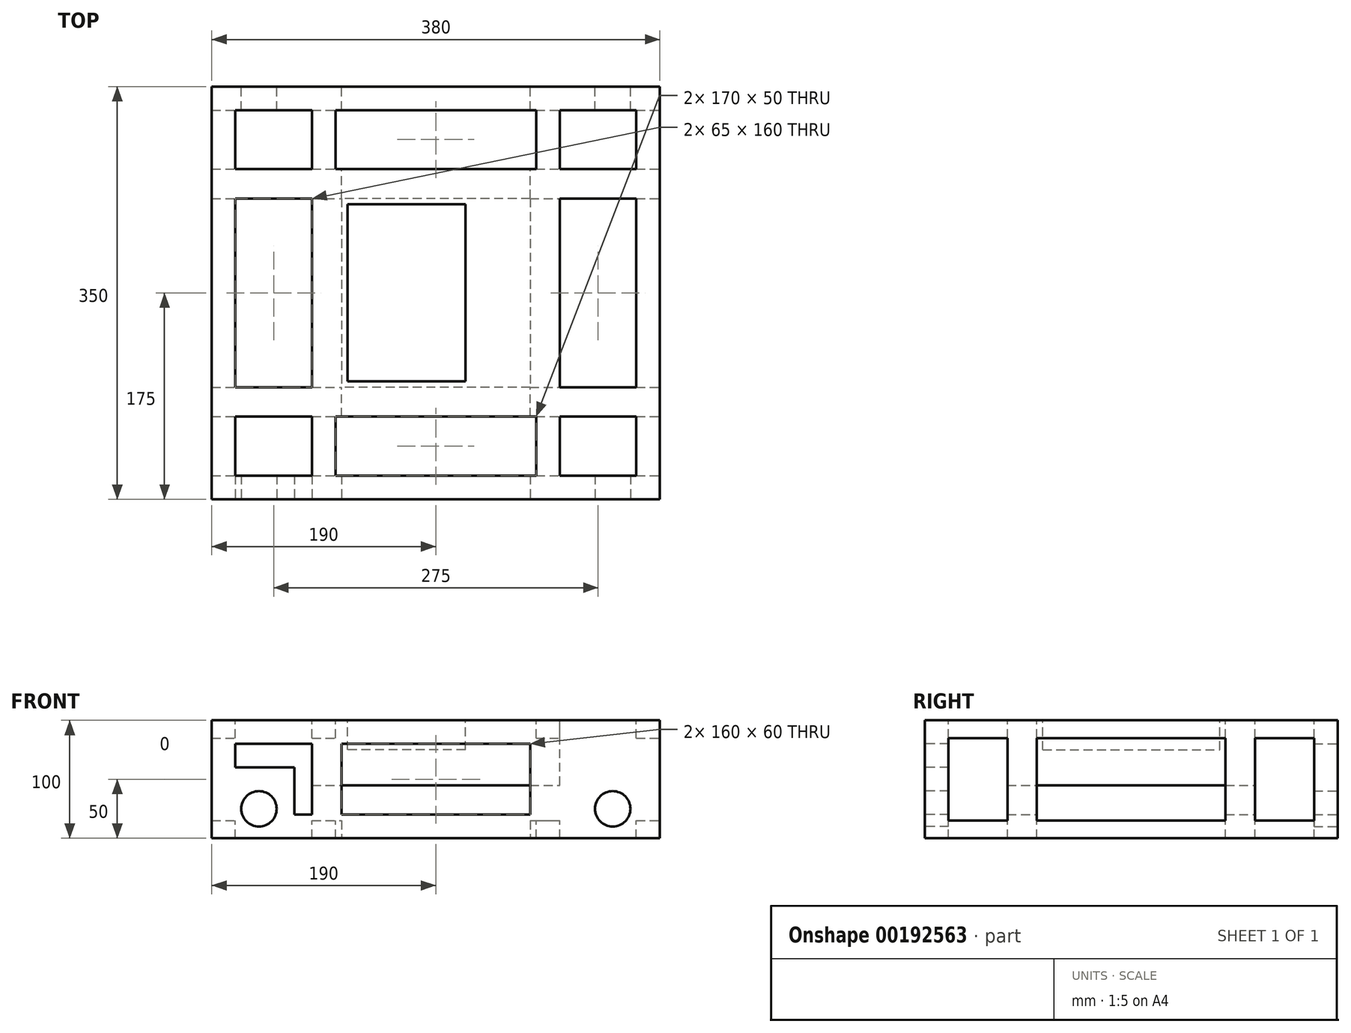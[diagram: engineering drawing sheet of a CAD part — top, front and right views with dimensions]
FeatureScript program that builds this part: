
annotation { "Feature Type Name" : "Feature", "Feature Type Description" : "" }
export const myFeature = defineFeature(function(context is Context, id is Id, definition is map)
    precondition{}
    {
        {
            var Q0;
            Q0=qCreatedBy(makeId("Top.planeOp"),FACE);
            var sketch = newSketch(context, id + "F0", { "sketchPlane" : qUnion([Q0])});
            skLineSegment(sketch, "E0.bottom", {"start": v(190, -175) * mm, "end": v(-190, -175) * mm});
            skLineSegment(sketch, "E0.top", {"start": v(190, 175) * mm, "end": v(-190, 175) * mm});
            skLineSegment(sketch, "E0.left", {"start": v(190, -175) * mm, "end": v(190, 175) * mm});
            skLineSegment(sketch, "E0.right", {"start": v(-190, -175) * mm, "end": v(-190, 175) * mm});
            skPoint(sketch, "E0.middle", {"position": v(0, 0) * mm});
            skSolve(sketch);
        }
        {
            var Q0;
            Q0 = qSketchRegion(id + "F0", true);
            extrude(context, id + "F1", {"entities" : qUnion([Q0]), "depth" : 100 * mm});
        }
        {
            var Q0;
            Q0=makeQuery(id+"F1.opExtrude","CAP_FACE",FACE,{"disambiguationData":[OSD([sQuery(id+"F0.wireOp",EDGE,"E0.bottom"),sQuery(id+"F0.wireOp",EDGE,"E0.top"),sQuery(id+"F0.wireOp",EDGE,"E0.left"),sQuery(id+"F0.wireOp",EDGE,"E0.right")])],"isStart":false});
            var sketch = newSketch(context, id + "F2", { "sketchPlane" : qUnion([Q0])});
            skLineSegment(sketch, "E1.bottom", {"start": v(-85, 155) * mm, "end": v(85, 155) * mm});
            skLineSegment(sketch, "E1.top", {"start": v(-85, 105) * mm, "end": v(85, 105) * mm});
            skLineSegment(sketch, "E1.left", {"start": v(-85, 155) * mm, "end": v(-85, 105) * mm});
            skLineSegment(sketch, "E1.right", {"start": v(85, 155) * mm, "end": v(85, 105) * mm});
            skLineSegment(sketch, "E2.bottom", {"start": v(105, 155) * mm, "end": v(170, 155) * mm});
            skLineSegment(sketch, "E2.top", {"start": v(105, 105) * mm, "end": v(170, 105) * mm});
            skLineSegment(sketch, "E2.left", {"start": v(105, 155) * mm, "end": v(105, 105) * mm});
            skLineSegment(sketch, "E2.right", {"start": v(170, 155) * mm, "end": v(170, 105) * mm});
            skLineSegment(sketch, "E3.bottom", {"start": v(105, 80) * mm, "end": v(170, 80) * mm});
            skLineSegment(sketch, "E3.top", {"start": v(105, -80) * mm, "end": v(170, -80) * mm});
            skLineSegment(sketch, "E3.left", {"start": v(105, 80) * mm, "end": v(105, -80) * mm});
            skLineSegment(sketch, "E3.right", {"start": v(170, 80) * mm, "end": v(170, -80) * mm});
            skLineSegment(sketch, "E4.bottom", {"start": v(105, -105) * mm, "end": v(170, -105) * mm});
            skLineSegment(sketch, "E4.top", {"start": v(105, -155) * mm, "end": v(170, -155) * mm});
            skLineSegment(sketch, "E4.left", {"start": v(105, -105) * mm, "end": v(105, -155) * mm});
            skLineSegment(sketch, "E4.right", {"start": v(170, -105) * mm, "end": v(170, -155) * mm});
            skLineSegment(sketch, "E5.bottom", {"start": v(85, -155) * mm, "end": v(-85, -155) * mm});
            skLineSegment(sketch, "E5.top", {"start": v(85, -105) * mm, "end": v(-85, -105) * mm});
            skLineSegment(sketch, "E5.left", {"start": v(85, -155) * mm, "end": v(85, -105) * mm});
            skLineSegment(sketch, "E5.right", {"start": v(-85, -155) * mm, "end": v(-85, -105) * mm});
            skLineSegment(sketch, "E6.bottom", {"start": v(-170, -105) * mm, "end": v(-105, -105) * mm});
            skLineSegment(sketch, "E6.top", {"start": v(-170, -155) * mm, "end": v(-105, -155) * mm});
            skLineSegment(sketch, "E6.left", {"start": v(-170, -105) * mm, "end": v(-170, -155) * mm});
            skLineSegment(sketch, "E6.right", {"start": v(-105, -105) * mm, "end": v(-105, -155) * mm});
            skLineSegment(sketch, "E7.bottom", {"start": v(-170, -80) * mm, "end": v(-105, -80) * mm});
            skLineSegment(sketch, "E7.top", {"start": v(-170, 80) * mm, "end": v(-105, 80) * mm});
            skLineSegment(sketch, "E7.left", {"start": v(-170, -80) * mm, "end": v(-170, 80) * mm});
            skLineSegment(sketch, "E7.right", {"start": v(-105, -80) * mm, "end": v(-105, 80) * mm});
            skLineSegment(sketch, "E8.bottom", {"start": v(-170, 155) * mm, "end": v(-105, 155) * mm});
            skLineSegment(sketch, "E8.top", {"start": v(-170, 105) * mm, "end": v(-105, 105) * mm});
            skLineSegment(sketch, "E8.left", {"start": v(-170, 155) * mm, "end": v(-170, 105) * mm});
            skLineSegment(sketch, "E8.right", {"start": v(-105, 155) * mm, "end": v(-105, 105) * mm});
            skSolve(sketch);
        }
        {
            var Q0;
            Q0 = qSketchRegion(id + "F2", true);
            extrude(context, id + "F3", {"entities" : qUnion([Q0]), "operationType" : NewBodyOperationType.REMOVE, "endBound" : BoundingType.THROUGH_ALL, "oppositeDirection" : true, "depth" : 25 * mm});
        }
        {
            var Q0;
            Q0=makeQuery(id+"F1.opExtrude","SWEPT_FACE",FACE,{"disambiguationData":[OSD([sQuery(id+"F0.wireOp",EDGE,"E0.left")])]});
            var sketch = newSketch(context, id + "F4", { "sketchPlane" : qUnion([Q0])});
            skLineSegment(sketch, "E9.bottom", {"start": v(-155, 85) * mm, "end": v(-105, 85) * mm});
            skLineSegment(sketch, "E9.top", {"start": v(-155, 15) * mm, "end": v(-105, 15) * mm});
            skLineSegment(sketch, "E9.left", {"start": v(-155, 85) * mm, "end": v(-155, 15) * mm});
            skLineSegment(sketch, "E9.right", {"start": v(-105, 85) * mm, "end": v(-105, 15) * mm});
            skLineSegment(sketch, "E10.bottom", {"start": v(-80, 85) * mm, "end": v(80, 85) * mm});
            skLineSegment(sketch, "E10.top", {"start": v(-80, 15) * mm, "end": v(80, 15) * mm});
            skLineSegment(sketch, "E10.left", {"start": v(-80, 85) * mm, "end": v(-80, 15) * mm});
            skLineSegment(sketch, "E10.right", {"start": v(80, 85) * mm, "end": v(80, 15) * mm});
            skLineSegment(sketch, "E11.bottom", {"start": v(105, 85) * mm, "end": v(155, 85) * mm});
            skLineSegment(sketch, "E11.top", {"start": v(105, 15) * mm, "end": v(155, 15) * mm});
            skLineSegment(sketch, "E11.left", {"start": v(105, 85) * mm, "end": v(105, 15) * mm});
            skLineSegment(sketch, "E11.right", {"start": v(155, 85) * mm, "end": v(155, 15) * mm});
            skSolve(sketch);
        }
        {
            var Q0;
            Q0 = qSketchRegion(id + "F4", true);
            extrude(context, id + "F5", {"entities" : qUnion([Q0]), "operationType" : NewBodyOperationType.REMOVE, "endBound" : BoundingType.THROUGH_ALL, "oppositeDirection" : true, "depth" : 25 * mm});
        }
        {
            var Q0;
            Q0=makeQuery(id+"F1.opExtrude","SWEPT_FACE",FACE,{"disambiguationData":[OSD([sQuery(id+"F0.wireOp",EDGE,"E0.top")])]});
            var sketch = newSketch(context, id + "F6", { "sketchPlane" : qUnion([Q0])});
            skSolve(sketch);
        }
        {
            var Q0;
            {var subQ0=sQuery(id+"F0.wireOp",EDGE,"E0.top");Q0=makeQuery(id+"F6.imprint","IMPRINT",FACE,{"disambiguationData":[TD([[makeQuery(id+"F6.imprint","IMPRINT",EDGE,{"derivedFrom":makeQuery(id+"F1.opExtrude","CAP_EDGE",EDGE,{"disambiguationData":[OSD([subQ0])],"isStart":true})}),1.0]])]});}
            var sketch = newSketch(context, id + "F7", { "sketchPlane" : qUnion([Q0])});
            skCircle(sketch, "E12", {"center": v(-150, 25) * mm, "radius": 15 * mm});
            skCircle(sketch, "E13", {"center": v(150, 25) * mm, "radius": 15 * mm});
            skSolve(sketch);
        }
        {
            var Q0;
            Q0 = qSketchRegion(id + "F7", true);
            extrude(context, id + "F8", {"entities" : qUnion([Q0]), "operationType" : NewBodyOperationType.REMOVE, "oppositeDirection" : true, "depth" : 25 * mm});
        }
        {
            var Q0;
            Q0=makeQuery(id+"F1.opExtrude","SWEPT_FACE",FACE,{"disambiguationData":[OSD([sQuery(id+"F0.wireOp",EDGE,"E0.bottom")])]});
            var sketch = newSketch(context, id + "F9", { "sketchPlane" : qUnion([Q0])});
            skCircle(sketch, "E14", {"center": v(-150, 25) * mm, "radius": 15 * mm});
            skCircle(sketch, "E15", {"center": v(150, 25) * mm, "radius": 15 * mm});
            skSolve(sketch);
        }
        {
            var Q0;
            Q0 = qSketchRegion(id + "F9", true);
            extrude(context, id + "F10", {"entities" : qUnion([Q0]), "operationType" : NewBodyOperationType.REMOVE, "oppositeDirection" : true, "depth" : 25 * mm});
        }
        {
            var Q0;
            {var subQ0=sQuery(id+"F0.wireOp",EDGE,"E0.top");Q0=makeQuery(id+"F6.imprint","IMPRINT",FACE,{"disambiguationData":[TD([[makeQuery(id+"F6.imprint","IMPRINT",EDGE,{"derivedFrom":makeQuery(id+"F1.opExtrude","CAP_EDGE",EDGE,{"disambiguationData":[OSD([subQ0])],"isStart":true})}),1.0]])]});}
            var sketch = newSketch(context, id + "F11", { "sketchPlane" : qUnion([Q0])});
            skLineSegment(sketch, "E16.bottom", {"start": v(80, 20) * mm, "end": v(-80, 20) * mm});
            skLineSegment(sketch, "E16.top", {"start": v(80, 80) * mm, "end": v(-80, 80) * mm});
            skLineSegment(sketch, "E16.left", {"start": v(80, 20) * mm, "end": v(80, 80) * mm});
            skLineSegment(sketch, "E16.right", {"start": v(-80, 20) * mm, "end": v(-80, 80) * mm});
            skPoint(sketch, "E16.middle", {"position": v(0, 50) * mm});
            skSolve(sketch);
        }
        {
            var Q0;
            Q0 = qSketchRegion(id + "F11", true);
            extrude(context, id + "F12", {"entities" : qUnion([Q0]), "operationType" : NewBodyOperationType.REMOVE, "oppositeDirection" : true, "depth" : 25 * mm});
        }
        {
            var Q0;
            Q0=makeQuery(id+"F1.opExtrude","SWEPT_FACE",FACE,{"disambiguationData":[OSD([sQuery(id+"F0.wireOp",EDGE,"E0.bottom")])]});
            var sketch = newSketch(context, id + "F13", { "sketchPlane" : qUnion([Q0])});
            skLineSegment(sketch, "E17.bottom", {"start": v(80, 20) * mm, "end": v(-80, 20) * mm});
            skLineSegment(sketch, "E17.top", {"start": v(80, 80) * mm, "end": v(-80, 80) * mm});
            skLineSegment(sketch, "E17.left", {"start": v(80, 20) * mm, "end": v(80, 80) * mm});
            skLineSegment(sketch, "E17.right", {"start": v(-80, 20) * mm, "end": v(-80, 80) * mm});
            skPoint(sketch, "E17.middle", {"position": v(0, 50) * mm});
            skSolve(sketch);
        }
        {
            var Q0;
            Q0 = qSketchRegion(id + "F13", true);
            extrude(context, id + "F14", {"entities" : qUnion([Q0]), "operationType" : NewBodyOperationType.REMOVE, "oppositeDirection" : true, "depth" : 25 * mm});
        }
        {
            var Q0;
            Q0=makeQuery(id+"F1.opExtrude","CAP_FACE",FACE,{"disambiguationData":[OSD([sQuery(id+"F0.wireOp",EDGE,"E0.bottom"),sQuery(id+"F0.wireOp",EDGE,"E0.top"),sQuery(id+"F0.wireOp",EDGE,"E0.left"),sQuery(id+"F0.wireOp",EDGE,"E0.right")])],"isStart":true});
            var sketch = newSketch(context, id + "F15", { "sketchPlane" : qUnion([Q0])});
            skLineSegment(sketch, "E18.bottom", {"start": v(80, -80) * mm, "end": v(-80, -80) * mm});
            skLineSegment(sketch, "E18.top", {"start": v(80, 80) * mm, "end": v(-80, 80) * mm});
            skLineSegment(sketch, "E18.left", {"start": v(80, -80) * mm, "end": v(80, 80) * mm});
            skLineSegment(sketch, "E18.right", {"start": v(-80, -80) * mm, "end": v(-80, 80) * mm});
            skPoint(sketch, "E18.middle", {"position": v(0, 0) * mm});
            skSolve(sketch);
        }
        {
            var Q0;
            Q0 = qSketchRegion(id + "F15", true);
            extrude(context, id + "F16", {"entities" : qUnion([Q0]), "operationType" : NewBodyOperationType.REMOVE, "oppositeDirection" : true, "depth" : 25 * mm});
        }
        {
            var Q0;
            Q0=makeQuery(id+"F5.boolean.opBoolean","COPY",FACE,{"disambiguationData":[TD([makeQuery(id+"F3.boolean.opBoolean","COPY",FACE,{"derivedFrom":makeQuery(id+"F3.opExtrude","SWEPT_FACE",FACE,{"disambiguationData":[OSD([sQuery(id+"F2.wireOp",EDGE,"E3.left")])]})})])],"derivedFrom":makeQuery(id+"F5.opExtrude","SWEPT_FACE",FACE,{"disambiguationData":[OSD([sQuery(id+"F4.wireOp",EDGE,"E10.bottom")])]})});
            var sketch = newSketch(context, id + "F17", { "sketchPlane" : qUnion([Q0])});
            skLineSegment(sketch, "E19.bottom", {"start": v(105, 105) * mm, "end": v(-105, 105) * mm});
            skLineSegment(sketch, "E19.top", {"start": v(105, -105) * mm, "end": v(-105, -105) * mm});
            skLineSegment(sketch, "E19.left", {"start": v(105, -105) * mm, "end": v(105, 105) * mm});
            skLineSegment(sketch, "E19.right", {"start": v(-105, -105) * mm, "end": v(-105, 105) * mm});
            skPoint(sketch, "E19.middle", {"position": v(0, 0) * mm});
            skSolve(sketch);
        }
        {
            var Q0;
            Q0 = qSketchRegion(id + "F17", true);
            extrude(context, id + "F18", {"entities" : qUnion([Q0]), "operationType" : NewBodyOperationType.ADD, "depth" : 40 * mm});
        }
        {
            var Q0;
            Q0=makeQuery(id+"F1.opExtrude","CAP_FACE",FACE,{"disambiguationData":[OSD([sQuery(id+"F0.wireOp",EDGE,"E0.bottom"),sQuery(id+"F0.wireOp",EDGE,"E0.top"),sQuery(id+"F0.wireOp",EDGE,"E0.left"),sQuery(id+"F0.wireOp",EDGE,"E0.right")])],"isStart":false});
            var sketch = newSketch(context, id + "F19", { "sketchPlane" : qUnion([Q0])});
            skLineSegment(sketch, "E20.bottom", {"start": v(25, -75) * mm, "end": v(-75, -75) * mm});
            skLineSegment(sketch, "E20.top", {"start": v(25, 75) * mm, "end": v(-75, 75) * mm});
            skLineSegment(sketch, "E20.left", {"start": v(25, -75) * mm, "end": v(25, 75) * mm});
            skLineSegment(sketch, "E20.right", {"start": v(-75, -75) * mm, "end": v(-75, 75) * mm});
            skPoint(sketch, "E20.middle", {"position": v(-25, 0) * mm});
            skSolve(sketch);
        }
        {
            var Q0;
            Q0 = qSketchRegion(id + "F19", true);
            extrude(context, id + "F20", {"entities" : qUnion([Q0]), "operationType" : NewBodyOperationType.REMOVE, "oppositeDirection" : true, "depth" : 25 * mm});
        }
        {
            var Q0;
            {var subQ0=sQuery(id+"F0.wireOp",EDGE,"E0.top");Q0=makeQuery(id+"F6.imprint","IMPRINT",FACE,{"disambiguationData":[TD([[makeQuery(id+"F6.imprint","IMPRINT",EDGE,{"derivedFrom":makeQuery(id+"F1.opExtrude","CAP_EDGE",EDGE,{"disambiguationData":[OSD([subQ0])],"isStart":true})}),1.0]])]});}
            var sketch = newSketch(context, id + "F21", { "sketchPlane" : qUnion([Q0])});
            skLineSegment(sketch, "E21.bottom", {"start": v(80, 20) * mm, "end": v(-80, 20) * mm});
            skLineSegment(sketch, "E21.top", {"start": v(80, 45) * mm, "end": v(-80, 45) * mm});
            skLineSegment(sketch, "E21.left", {"start": v(80, 20) * mm, "end": v(80, 45) * mm});
            skLineSegment(sketch, "E21.right", {"start": v(-80, 20) * mm, "end": v(-80, 45) * mm});
            skPoint(sketch, "E21.middle", {"position": v(0, 32.5) * mm});
            skSolve(sketch);
        }
        {
            var Q0;
            Q0 = qSketchRegion(id + "F21", true);
            extrude(context, id + "F22", {"entities" : qUnion([Q0]), "operationType" : NewBodyOperationType.REMOVE, "endBound" : BoundingType.THROUGH_ALL, "oppositeDirection" : true, "depth" : 25 * mm});
        }
        {
            var Q0;
            Q0=makeQuery(id+"F1.opExtrude","SWEPT_FACE",FACE,{"disambiguationData":[OSD([sQuery(id+"F0.wireOp",EDGE,"E0.bottom")])]});
            var sketch = newSketch(context, id + "F23", { "sketchPlane" : qUnion([Q0])});
            skLineSegment(sketch, "E22", {"start": v(-170, 80) * mm, "end": v(-105, 80) * mm});
            skLineSegment(sketch, "E23", {"start": v(-105, 80) * mm, "end": v(-105, 20) * mm});
            skLineSegment(sketch, "E24", {"start": v(-105, 20) * mm, "end": v(-120, 20) * mm});
            skLineSegment(sketch, "E25", {"start": v(-120, 20) * mm, "end": v(-120, 60) * mm});
            skLineSegment(sketch, "E26", {"start": v(-120, 60) * mm, "end": v(-170, 60) * mm});
            skLineSegment(sketch, "E27", {"start": v(-170, 60) * mm, "end": v(-170, 80) * mm});
            skSolve(sketch);
        }
        {
            var Q0;
            Q0 = qSketchRegion(id + "F23", true);
            extrude(context, id + "F24", {"entities" : qUnion([Q0]), "operationType" : NewBodyOperationType.REMOVE, "oppositeDirection" : true, "depth" : 25 * mm});
        }
    });
